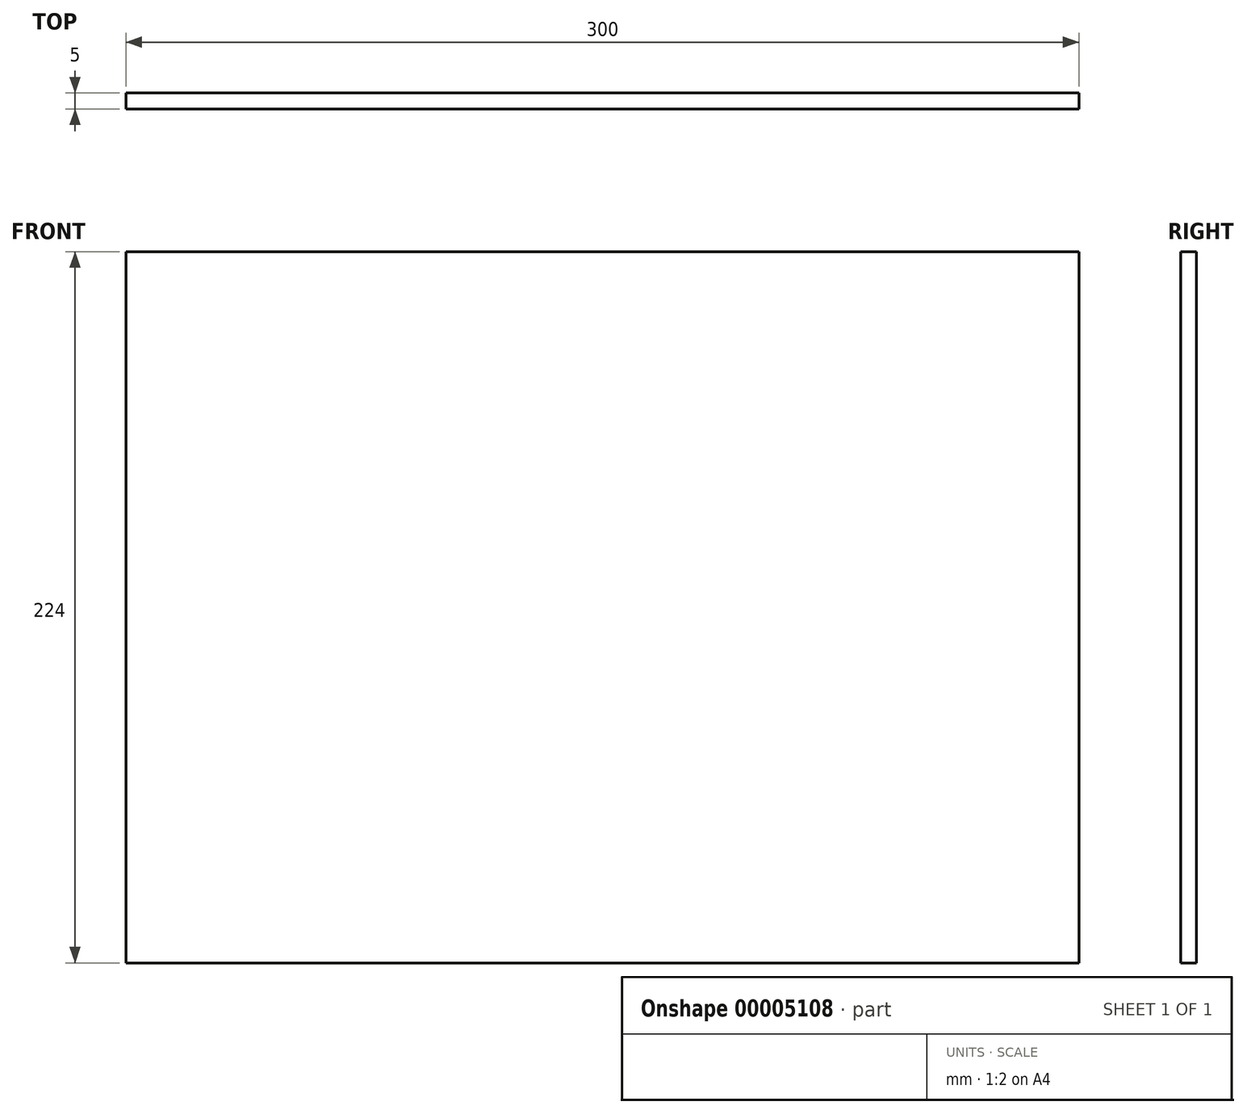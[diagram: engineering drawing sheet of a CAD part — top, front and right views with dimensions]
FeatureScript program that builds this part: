
annotation { "Feature Type Name" : "Feature", "Feature Type Description" : "" }
export const myFeature = defineFeature(function(context is Context, id is Id, definition is map)
    precondition{}
    {
        {
            var Q0;
            Q0=qCreatedBy(makeId("Front.planeOp"),FACE);
            var sketch = newSketch(context, id + "F0", { "sketchPlane" : qUnion([Q0])});
            skLineSegment(sketch, "E0.bottom", {"start": v(-151.36, 114.68) * mm, "end": v(148.64, 114.68) * mm});
            skLineSegment(sketch, "E0.top", {"start": v(-151.36, -109.32) * mm, "end": v(148.64, -109.32) * mm});
            skLineSegment(sketch, "E0.left", {"start": v(-151.36, 114.68) * mm, "end": v(-151.36, -109.32) * mm});
            skLineSegment(sketch, "E0.right", {"start": v(148.64, 114.68) * mm, "end": v(148.64, -109.32) * mm});
            skSolve(sketch);
        }
        {
            var Q0;
            Q0=makeQuery(id+"F0.imprint","IMPRINT",FACE,{"disambiguationData":[TD([[makeQuery(id+"F0.imprint","IMPRINT",EDGE,{"derivedFrom":sQuery(id+"F0.wireOp",EDGE,"E0.bottom")}),-1.0]])]});
            extrude(context, id + "F1", {"entities" : qUnion([Q0]), "depth" : 5 * mm});
        }
    });
